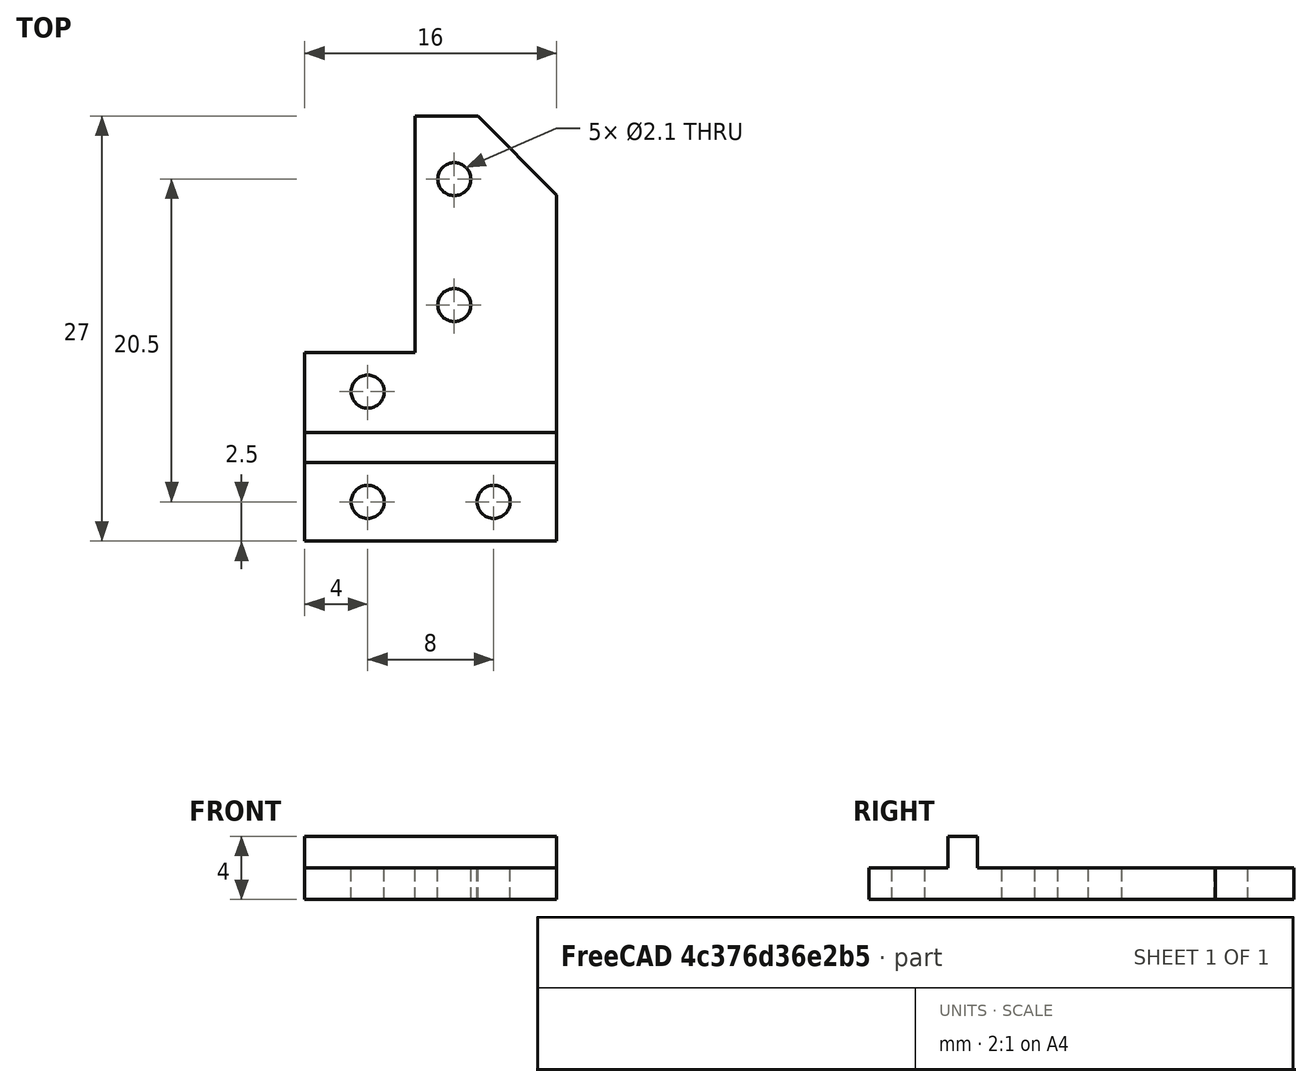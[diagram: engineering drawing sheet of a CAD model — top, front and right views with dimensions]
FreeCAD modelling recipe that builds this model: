
FCSTD DOCUMENT  (FreeCAD 0.15R4671 (Git))
Label: inter_mx-18_fastener_end
License: CC-BY 3.0
LicenseURL: http://creativecommons.org/licenses/by/3.0/
objects: Part::Cylinder×5, Part::MultiFuse×5, Part::Box×3, Part::Chamfer×1, Part::Cut×1
note: 15 computed .brp shape members not serialized (recipe doc carries the construction recipe); baked Part::Feature solids carry a one-line shape summary decoded from their .brp

FEATURE [Part::Box] Box  label="Cube"
  Height = 2
  Length = 16
  Width = 12
FEATURE [Part::Cylinder] Cylinder
  Angle = 360
  Height = 10
  Placement = pos=(0,2.5,-3) rot=(0,0,1;0rad)
  Radius = 1.05
FEATURE [Part::Cylinder] Cylinder001
  Angle = 360
  Height = 10
  Placement = pos=(8,2.5,-3) rot=(0,0,1;0rad)
  Radius = 1.05
FEATURE [Part::Box] Box001  label="Cube001"
  Height = 2
  Length = 16
  Placement = pos=(0,5,2) rot=(0,0,1;0rad)
  Width = 1.9
FEATURE [Part::MultiFuse] Fusion002
  Shapes = -> [Box001,Box]
FEATURE [Part::MultiFuse] Fusion
  Placement = pos=(4,0,0) rot=(0,0,1;0rad)
  Shapes = -> [Cylinder,Cylinder001]
FEATURE [Part::Cylinder] Cylinder002
  Angle = 360
  Height = 10
  Placement = pos=(4,9.5,-3) rot=(0,0,1;0rad)
  Radius = 1.05
FEATURE [Part::Box] Box002  label="Cube002"
  Height = 2
  Length = 9
  Placement = pos=(7,12,0) rot=(0,0,1;0rad)
  Width = 15
FEATURE [Part::Cylinder] Cylinder003
  Angle = 360
  Height = 10
  Placement = pos=(9.5,15,-3) rot=(0,0,1;0rad)
  Radius = 1.05
FEATURE [Part::Cylinder] Cylinder004
  Angle = 360
  Height = 10
  Placement = pos=(9.5,23,-3) rot=(0,0,1;0rad)
  Radius = 1.05
FEATURE [Part::Chamfer] Chamfer
  Base = -> Box002
  Edges = 1 edges r=5: [Edge7]
FEATURE [Part::MultiFuse] Fusion003
  Shapes = -> [Cylinder004,Cylinder002,Cylinder003]
FEATURE [Part::MultiFuse] Fusion004
  Shapes = -> [Chamfer,Fusion002]
FEATURE [Part::MultiFuse] Fusion005
  Shapes = -> [Fusion,Fusion003]
FEATURE [Part::Cut] Cut
  Base = -> Fusion004
  Tool = -> Fusion005
